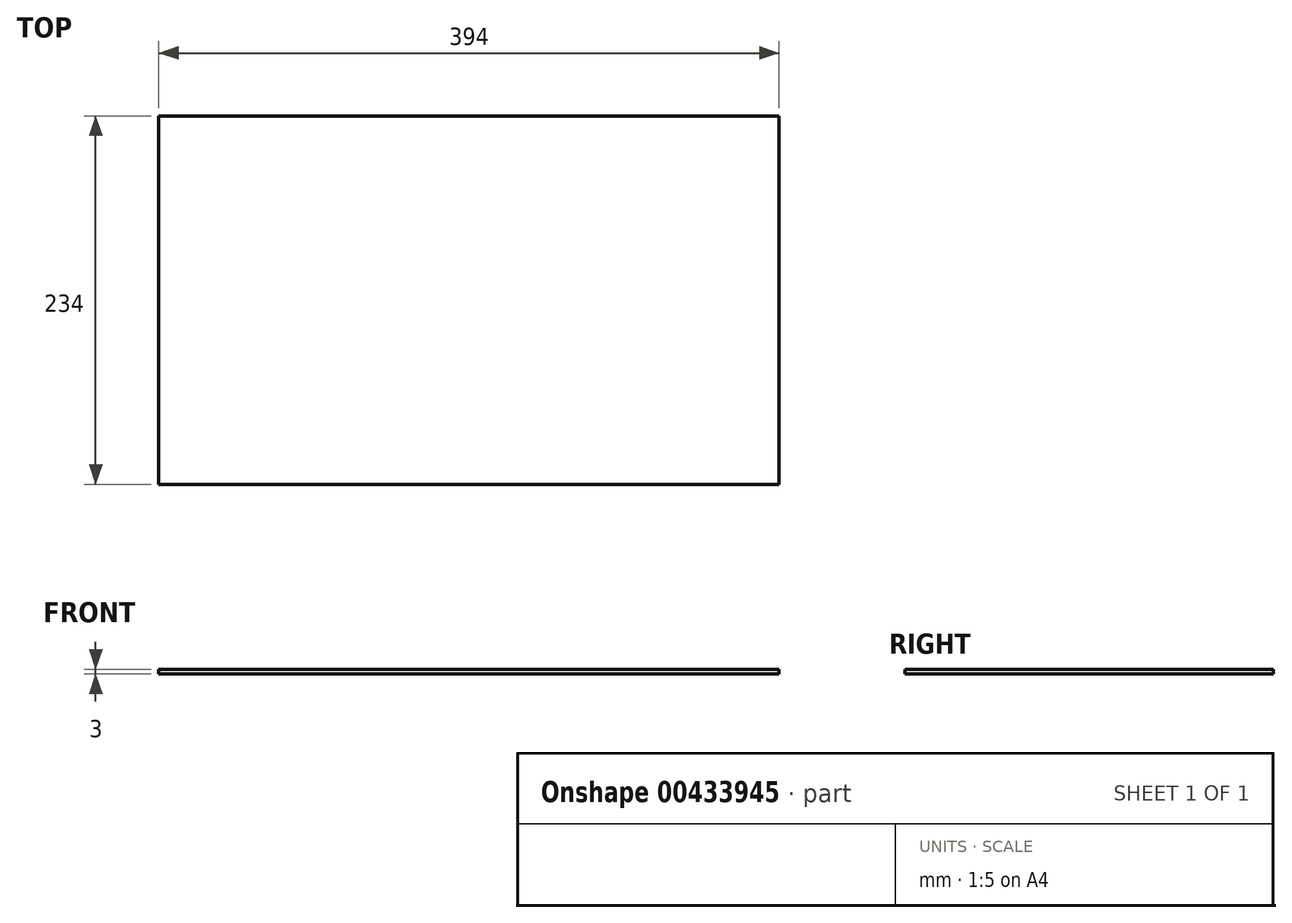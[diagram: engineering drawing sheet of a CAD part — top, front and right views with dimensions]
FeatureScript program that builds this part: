
annotation { "Feature Type Name" : "Feature", "Feature Type Description" : "" }
export const myFeature = defineFeature(function(context is Context, id is Id, definition is map)
    precondition{}
    {
        {
            var Q0;
            Q0=qCreatedBy(makeId("Top.planeOp"),FACE);
            var sketch = newSketch(context, id + "F0", { "sketchPlane" : qUnion([Q0])});
            skLineSegment(sketch, "E0.bottom", {"start": v(197, -117) * mm, "end": v(-197, -117) * mm});
            skLineSegment(sketch, "E0.top", {"start": v(197, 117) * mm, "end": v(-197, 117) * mm});
            skLineSegment(sketch, "E0.left", {"start": v(197, -117) * mm, "end": v(197, 117) * mm});
            skLineSegment(sketch, "E0.right", {"start": v(-197, -117) * mm, "end": v(-197, 117) * mm});
            skPoint(sketch, "E0.middle", {"position": v(0, 0) * mm});
            skSolve(sketch);
        }
        {
            var Q0;
            Q0=makeQuery(id+"F0.imprint","IMPRINT",FACE,{"disambiguationData":[TD([[makeQuery(id+"F0.imprint","IMPRINT",EDGE,{"derivedFrom":sQuery(id+"F0.wireOp",EDGE,"E0.bottom")}),-1.0]])]});
            extrude(context, id + "F1", {"entities" : qUnion([Q0]), "depth" : 3 * mm});
        }
    });
